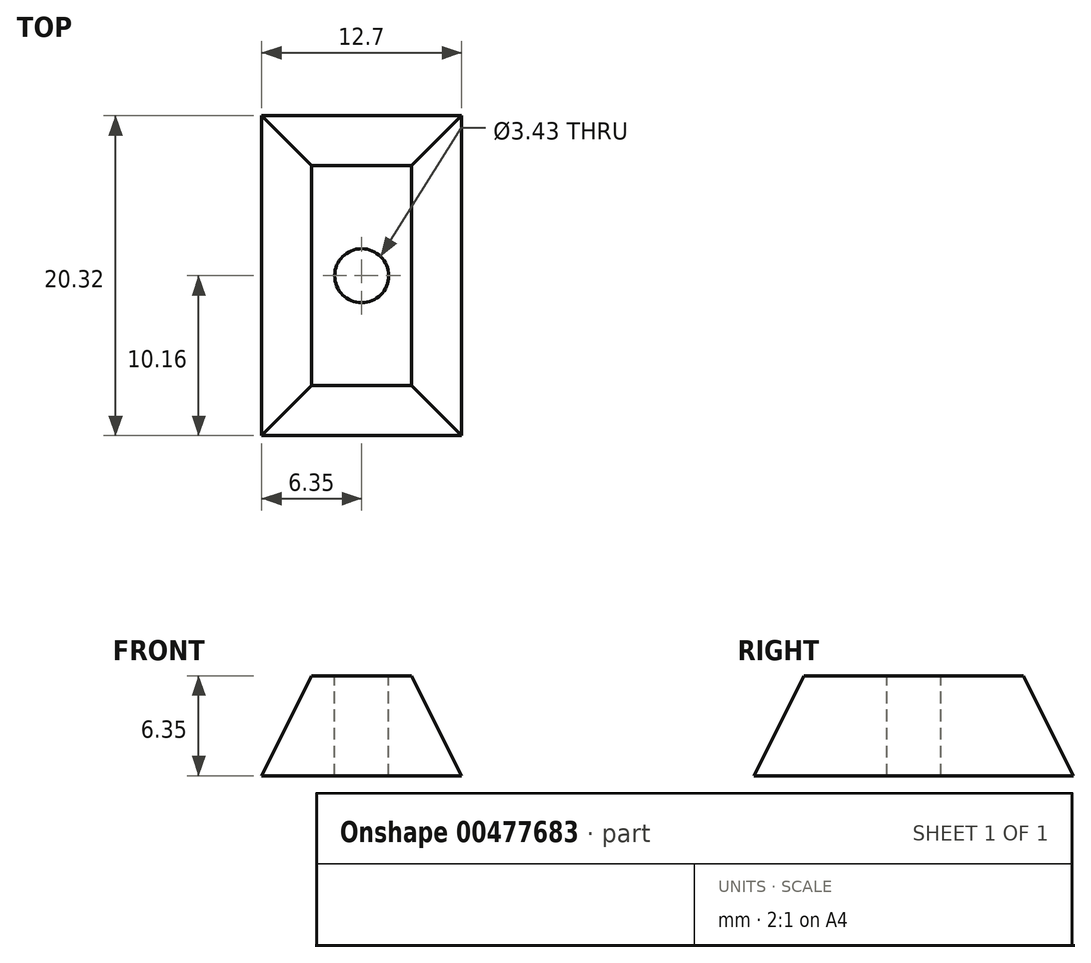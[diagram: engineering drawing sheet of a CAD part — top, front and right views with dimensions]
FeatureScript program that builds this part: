
annotation { "Feature Type Name" : "Feature", "Feature Type Description" : "" }
export const myFeature = defineFeature(function(context is Context, id is Id, definition is map)
    precondition{}
    {
        {
            var Q0;
            Q0=qCreatedBy(makeId("Front.planeOp"),FACE);
            var sketch = newSketch(context, id + "F0", { "sketchPlane" : qUnion([Q0])});
            skLineSegment(sketch, "E0.MirrorCS", {"start": v(-3.17, 6.35) * mm, "end": v(0, 6.35) * mm});
            skLineSegment(sketch, "E1.MirrorCS", {"start": v(-3.17, 6.35) * mm, "end": v(-6.35, 0) * mm});
            skLineSegment(sketch, "E2.MirrorCS", {"start": v(-6.35, 0) * mm, "end": v(0, 0) * mm});
            skLineSegment(sketch, "E3.MirrorCS", {"start": v(3.17, 6.35) * mm, "end": v(0, 6.35) * mm});
            skLineSegment(sketch, "E4.MirrorCS", {"start": v(3.17, 6.35) * mm, "end": v(6.35, 0) * mm});
            skLineSegment(sketch, "E5.MirrorCS", {"start": v(6.35, 0) * mm, "end": v(0, 0) * mm});
            skSolve(sketch);
        }
        {
            var Q0;
            Q0 = qSketchRegion(id + "F0", true);
            extrude(context, id + "F1", {"entities" : qUnion([Q0]), "endBound" : BoundingType.SYMMETRIC, "depth" : 20.32 * mm, "offsetDistance" : 25.4 * mm});
        }
        {
            var Q0;
            Q0=qCreatedBy(makeId("Right.planeOp"),FACE);
            var sketch = newSketch(context, id + "F2", { "sketchPlane" : qUnion([Q0])});
            skLineSegment(sketch, "E6.MirrorCS", {"start": v(-10.16, 0) * mm, "end": v(-10.16, 6.35) * mm});
            skLineSegment(sketch, "E7.MirrorCS", {"start": v(0, 0) * mm, "end": v(-10.16, 0) * mm});
            skLineSegment(sketch, "E8", {"start": v(0, 0) * mm, "end": v(0, 11.3) * mm, "construction": true});
            skLineSegment(sketch, "E9", {"start": v(-10.16, 6.35) * mm, "end": v(10.16, 6.35) * mm});
            skLineSegment(sketch, "E10", {"start": v(-10.16, 0) * mm, "end": v(-6.98, 6.35) * mm});
            skLineSegment(sketch, "E11.MirrorCS", {"start": v(0, 0) * mm, "end": v(10.16, 0) * mm});
            skLineSegment(sketch, "E12.MirrorCS", {"start": v(10.16, 0) * mm, "end": v(10.16, 6.35) * mm});
            skLineSegment(sketch, "E13.MirrorCS", {"start": v(10.16, 0) * mm, "end": v(6.98, 6.35) * mm});
            skSolve(sketch);
        }
        {
            var Q0;
            {var subQ0=sQuery(id+"F2.wireOp",EDGE,"E6.MirrorCS");Q0=makeQuery(id+"F2.imprint","IMPRINT",FACE,{"disambiguationData":[TD([[makeQuery(id+"F2.imprint","IMPRINT",EDGE,{"derivedFrom":subQ0}),-1.0]])]});}
            var Q1;
            {var subQ0=sQuery(id+"F2.wireOp",EDGE,"E12.MirrorCS");Q1=makeQuery(id+"F2.imprint","IMPRINT",FACE,{"disambiguationData":[TD([[makeQuery(id+"F2.imprint","IMPRINT",EDGE,{"derivedFrom":subQ0}),1.0]])]});}
            extrude(context, id + "F3", {"entities" : qUnion([Q0, Q1]), "operationType" : NewBodyOperationType.REMOVE, "endBound" : BoundingType.SYMMETRIC, "oppositeDirection" : true, "depth" : 25.4 * mm, "offsetDistance" : 25.4 * mm});
        }
        {
            var Q0;
            Q0=makeQuery(id+"F1.opExtrude","SWEPT_FACE",FACE,{"disambiguationData":[OSD([sQuery(id+"F0.wireOp",EDGE,"E0.MirrorCS"),sQuery(id+"F0.wireOp",EDGE,"E3.MirrorCS")])]});
            var sketch = newSketch(context, id + "F4", { "sketchPlane" : qUnion([Q0])});
            skPoint(sketch, "E14", {"position": v(0, 0) * mm});
            skSolve(sketch);
        }
        {
            var Q0;
            Q0=sQuery(id+"F4.wireOp",VERTEX,"E14");
            var Q1;
            Q1=makeQuery(id+"F1.opExtrude","SWEPT_BODY",BODY,{"disambiguationData":[OSD([sQuery(id+"F0.wireOp",EDGE,"E0.MirrorCS"),sQuery(id+"F0.wireOp",EDGE,"E1.MirrorCS"),sQuery(id+"F0.wireOp",EDGE,"E2.MirrorCS"),sQuery(id+"F0.wireOp",EDGE,"E3.MirrorCS"),sQuery(id+"F0.wireOp",EDGE,"E4.MirrorCS"),sQuery(id+"F0.wireOp",EDGE,"E5.MirrorCS")])]});
            hole(context, id + "F5", {"style" : HoleStyle.SIMPLE, "endStyle" : HoleEndStyle.THROUGH, "holeDiameter" : 3.43 * mm, "majorDiameter" : 6.35 * mm, "isTappedThrough" : true, "tappedDepth" : 12.7 * mm, "tapClearance" : 3, "locations" : qUnion([Q0]), "scope" : qUnion([Q1])});
        }
    });
